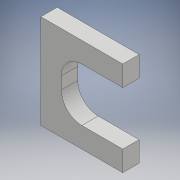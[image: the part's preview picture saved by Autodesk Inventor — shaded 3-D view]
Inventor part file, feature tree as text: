
AUTODESK INVENTOR PART (.ipt)
format: ipt  version: 2017 (Build 210142000, 142)  size: 104,448 bytes
history: native  units: mm
features: extrude x1, sketch x1
ambient origin geometry x8: Origin, YZ Plane, XZ Plane, XY Plane, X Axis, Y Axis, Z Axis, Center Point
bodies: Solid1 (feature_tree)
feature tree (2):
  extrude  "Extrusion1"  Depth=13.0mm
  sketch  "Sketch1"  dims[d0=15.0mm d1=13.0mm d2=5.0mm d3=5.0mm d4=5.0mm d5=4.0mm d6=0.0mm]
